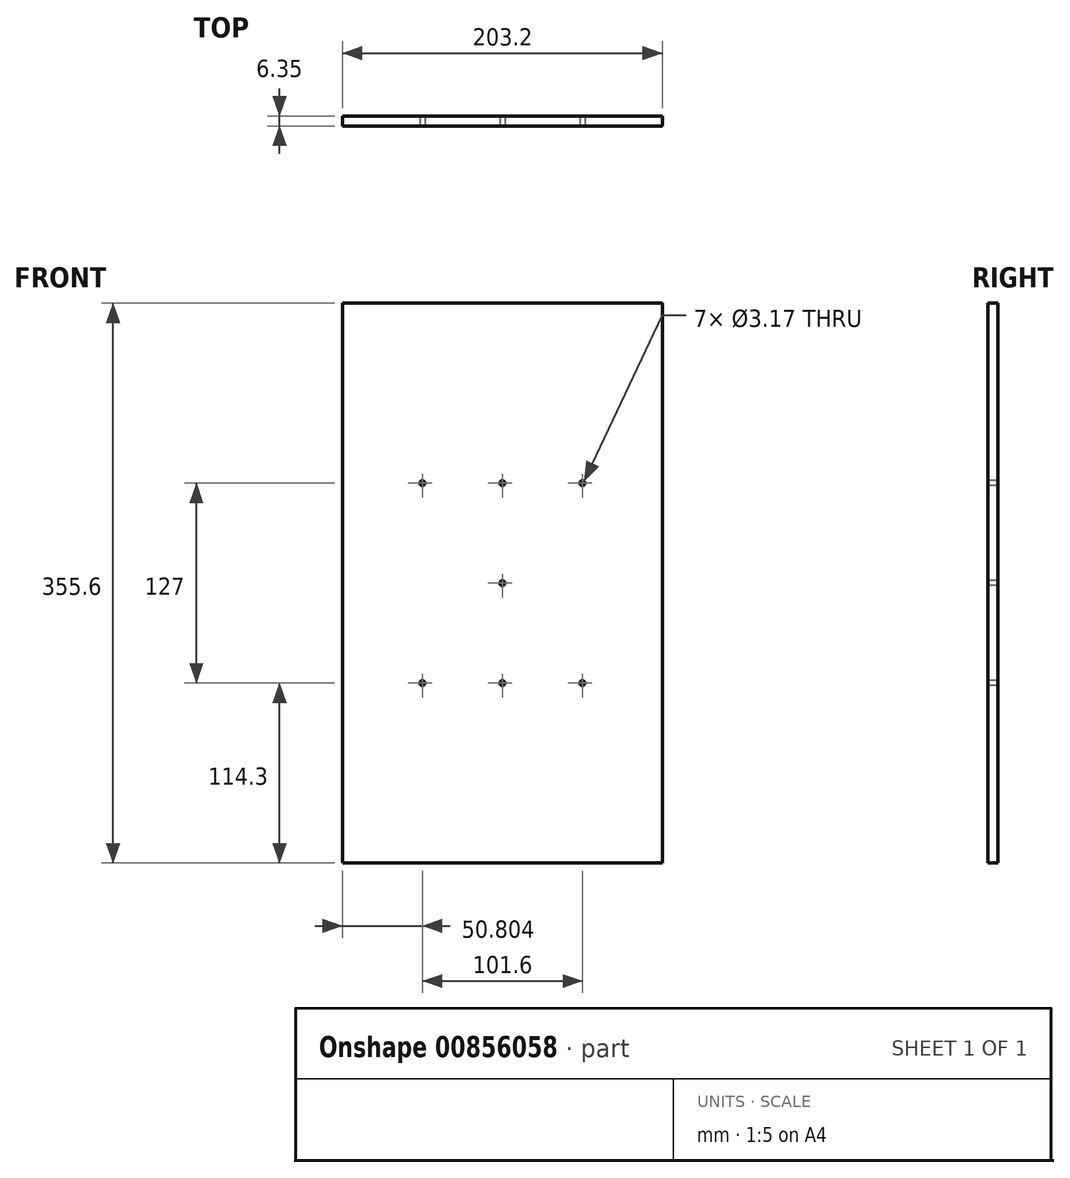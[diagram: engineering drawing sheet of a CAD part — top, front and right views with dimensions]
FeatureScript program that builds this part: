
annotation { "Feature Type Name" : "Feature", "Feature Type Description" : "" }
export const myFeature = defineFeature(function(context is Context, id is Id, definition is map)
    precondition{}
    {
        {
            var Q0;
            Q0=qCreatedBy(makeId("Front.planeOp"),FACE);
            var sketch = newSketch(context, id + "F0", { "sketchPlane" : qUnion([Q0])});
            skLineSegment(sketch, "E0.bottom", {"start": v(-103.34, 277.83) * mm, "end": v(99.86, 277.83) * mm});
            skLineSegment(sketch, "E0.top", {"start": v(-103.34, -77.77) * mm, "end": v(99.86, -77.77) * mm});
            skLineSegment(sketch, "E0.left", {"start": v(-103.34, 277.83) * mm, "end": v(-103.34, -77.77) * mm});
            skLineSegment(sketch, "E0.right", {"start": v(99.86, 277.83) * mm, "end": v(99.86, -77.77) * mm});
            skSolve(sketch);
        }
        {
            var Q0;
            Q0=makeQuery(id+"F0.imprint","IMPRINT",FACE,{"disambiguationData":[TD([[makeQuery(id+"F0.imprint","IMPRINT",EDGE,{"derivedFrom":sQuery(id+"F0.wireOp",EDGE,"E0.bottom")}),-1.0]])]});
            extrude(context, id + "F1", {"entities" : qUnion([Q0]), "depth" : 6.35 * mm, "offsetDistance" : 25.4 * mm});
        }
        {
            var Q0;
            Q0=makeQuery(id+"F1.opExtrude","CAP_FACE",FACE,{"disambiguationData":[OSD([sQuery(id+"F0.wireOp",EDGE,"E0.bottom"),sQuery(id+"F0.wireOp",EDGE,"E0.top"),sQuery(id+"F0.wireOp",EDGE,"E0.left"),sQuery(id+"F0.wireOp",EDGE,"E0.right")])],"isStart":false});
            var sketch = newSketch(context, id + "F2", { "sketchPlane" : qUnion([Q0])});
            skCircle(sketch, "E1", {"center": v(-1.74, 100.03) * mm, "radius": 1.59 * mm});
            skLineSegment(sketch, "E2", {"start": v(-1.74, 100.03) * mm, "end": v(-103.34, 100.03) * mm});
            skLineSegment(sketch, "E3", {"start": v(-1.74, 100.03) * mm, "end": v(99.86, 100.03) * mm});
            skCircle(sketch, "E4", {"center": v(-1.74, 163.53) * mm, "radius": 1.59 * mm});
            skCircle(sketch, "E5", {"center": v(-1.74, 36.53) * mm, "radius": 1.59 * mm});
            skLineSegment(sketch, "E6", {"start": v(-1.74, 163.53) * mm, "end": v(-1.74, 100.03) * mm});
            skLineSegment(sketch, "E7", {"start": v(-1.74, 100.03) * mm, "end": v(-1.74, 36.53) * mm});
            skCircle(sketch, "E8", {"center": v(-52.54, 163.53) * mm, "radius": 1.59 * mm});
            skCircle(sketch, "E9", {"center": v(49.06, 163.53) * mm, "radius": 1.59 * mm});
            skCircle(sketch, "E10", {"center": v(-52.54, 36.53) * mm, "radius": 1.59 * mm});
            skCircle(sketch, "E11", {"center": v(49.06, 36.53) * mm, "radius": 1.59 * mm});
            skLineSegment(sketch, "E12", {"start": v(-52.54, 163.53) * mm, "end": v(-103.34, 163.53) * mm});
            skLineSegment(sketch, "E13", {"start": v(-52.54, 163.53) * mm, "end": v(-1.74, 163.53) * mm});
            skLineSegment(sketch, "E14", {"start": v(-1.74, 163.53) * mm, "end": v(49.06, 163.53) * mm});
            skLineSegment(sketch, "E15", {"start": v(49.06, 163.53) * mm, "end": v(99.86, 163.53) * mm});
            skLineSegment(sketch, "E16", {"start": v(-52.54, 36.53) * mm, "end": v(-103.34, 36.53) * mm});
            skLineSegment(sketch, "E17", {"start": v(-52.54, 36.53) * mm, "end": v(-1.74, 36.53) * mm});
            skLineSegment(sketch, "E18", {"start": v(-1.74, 36.53) * mm, "end": v(49.06, 36.53) * mm});
            skLineSegment(sketch, "E19", {"start": v(49.06, 36.53) * mm, "end": v(99.86, 36.53) * mm});
            skLineSegment(sketch, "E20", {"start": v(-1.74, 163.53) * mm, "end": v(-1.74, 277.83) * mm});
            skLineSegment(sketch, "E21", {"start": v(-1.74, 36.53) * mm, "end": v(-1.74, -77.77) * mm});
            skSolve(sketch);
        }
        {
            var Q0;
            {var subQ0=sQuery(id+"F2.wireOp",EDGE,"E12");var subQ1=sQuery(id+"F2.wireOp",EDGE,"E8");var subQ2=makeQuery(id+"F2.imprint","INTERSECT",VERTEX,{"derivedFrom":[subQ1,subQ0]});Q0=makeQuery(id+"F2.imprint","IMPRINT",FACE,{"disambiguationData":[TD([[makeQuery(id+"F2.imprint","IMPRINT",EDGE,{"disambiguationData":[TD([[subQ2,1.0]])],"derivedFrom":subQ1}),1.0]])]});}
            var Q1;
            {var subQ0=sQuery(id+"F2.wireOp",EDGE,"E12");var subQ1=sQuery(id+"F2.wireOp",EDGE,"E8");var subQ2=makeQuery(id+"F2.imprint","INTERSECT",VERTEX,{"derivedFrom":[subQ1,subQ0]});Q1=makeQuery(id+"F2.imprint","IMPRINT",FACE,{"disambiguationData":[TD([[makeQuery(id+"F2.imprint","IMPRINT",EDGE,{"disambiguationData":[TD([[subQ2,-1.0]])],"derivedFrom":subQ1}),1.0]])]});}
            var Q2;
            {var subQ0=sQuery(id+"F2.wireOp",EDGE,"gXuljh3P-2iaE-ET4M-0B0z-znNCCFgcD3jr");var subQ1=sQuery(id+"F2.wireOp",EDGE,"E4");var subQ2=makeQuery(id+"F2.imprint","INTERSECT",VERTEX,{"derivedFrom":[subQ1,subQ0]});Q2=makeQuery(id+"F2.imprint","IMPRINT",FACE,{"disambiguationData":[TD([[makeQuery(id+"F2.imprint","IMPRINT",EDGE,{"disambiguationData":[TD([[subQ2,1.0]])],"derivedFrom":subQ1}),1.0]])]});}
            var Q3;
            {var subQ0=sQuery(id+"F2.wireOp",EDGE,"gXuljh3P-2iaE-ET4M-0B0z-znNCCFgcD3jr");var subQ1=sQuery(id+"F2.wireOp",EDGE,"E4");var subQ2=makeQuery(id+"F2.imprint","INTERSECT",VERTEX,{"derivedFrom":[subQ1,subQ0]});Q3=makeQuery(id+"F2.imprint","IMPRINT",FACE,{"disambiguationData":[TD([[makeQuery(id+"F2.imprint","IMPRINT",EDGE,{"disambiguationData":[TD([[subQ2,-1.0]])],"derivedFrom":subQ1}),1.0]])]});}
            var Q4;
            {var subQ0=sQuery(id+"F2.wireOp",EDGE,"E13");var subQ1=sQuery(id+"F2.wireOp",EDGE,"E4");var subQ2=makeQuery(id+"F2.imprint","INTERSECT",VERTEX,{"derivedFrom":[subQ1,subQ0]});Q4=makeQuery(id+"F2.imprint","IMPRINT",FACE,{"disambiguationData":[TD([[makeQuery(id+"F2.imprint","IMPRINT",EDGE,{"disambiguationData":[TD([[subQ2,-1.0]])],"derivedFrom":subQ1}),1.0]])]});}
            var Q5;
            {var subQ0=sQuery(id+"F2.wireOp",EDGE,"E14");var subQ1=sQuery(id+"F2.wireOp",EDGE,"E4");var subQ2=makeQuery(id+"F2.imprint","INTERSECT",VERTEX,{"derivedFrom":[subQ1,subQ0]});Q5=makeQuery(id+"F2.imprint","IMPRINT",FACE,{"disambiguationData":[TD([[makeQuery(id+"F2.imprint","IMPRINT",EDGE,{"disambiguationData":[TD([[subQ2,1.0]])],"derivedFrom":subQ1}),1.0]])]});}
            var Q6;
            {var subQ0=sQuery(id+"F2.wireOp",EDGE,"E14");var subQ1=sQuery(id+"F2.wireOp",EDGE,"E9");var subQ2=makeQuery(id+"F2.imprint","INTERSECT",VERTEX,{"derivedFrom":[subQ1,subQ0]});Q6=makeQuery(id+"F2.imprint","IMPRINT",FACE,{"disambiguationData":[TD([[makeQuery(id+"F2.imprint","IMPRINT",EDGE,{"disambiguationData":[TD([[subQ2,1.0]])],"derivedFrom":subQ1}),1.0]])]});}
            var Q7;
            {var subQ0=sQuery(id+"F2.wireOp",EDGE,"E14");var subQ1=sQuery(id+"F2.wireOp",EDGE,"E9");var subQ2=makeQuery(id+"F2.imprint","INTERSECT",VERTEX,{"derivedFrom":[subQ1,subQ0]});Q7=makeQuery(id+"F2.imprint","IMPRINT",FACE,{"disambiguationData":[TD([[makeQuery(id+"F2.imprint","IMPRINT",EDGE,{"disambiguationData":[TD([[subQ2,-1.0]])],"derivedFrom":subQ1}),1.0]])]});}
            var Q8;
            {var subQ0=sQuery(id+"F2.wireOp",EDGE,"E6");var subQ1=sQuery(id+"F2.wireOp",EDGE,"E1");var subQ2=makeQuery(id+"F2.imprint","INTERSECT",VERTEX,{"derivedFrom":[subQ1,subQ0]});Q8=makeQuery(id+"F2.imprint","IMPRINT",FACE,{"disambiguationData":[TD([[makeQuery(id+"F2.imprint","IMPRINT",EDGE,{"disambiguationData":[TD([[subQ2,-1.0]])],"derivedFrom":subQ1}),1.0]])]});}
            var Q9;
            {var subQ0=sQuery(id+"F2.wireOp",EDGE,"E6");var subQ1=sQuery(id+"F2.wireOp",EDGE,"E1");var subQ2=makeQuery(id+"F2.imprint","INTERSECT",VERTEX,{"derivedFrom":[subQ1,subQ0]});Q9=makeQuery(id+"F2.imprint","IMPRINT",FACE,{"disambiguationData":[TD([[makeQuery(id+"F2.imprint","IMPRINT",EDGE,{"disambiguationData":[TD([[subQ2,1.0]])],"derivedFrom":subQ1}),1.0]])]});}
            var Q10;
            {var subQ0=sQuery(id+"F2.wireOp",EDGE,"E3");var subQ1=sQuery(id+"F2.wireOp",EDGE,"E1");var subQ2=makeQuery(id+"F2.imprint","INTERSECT",VERTEX,{"derivedFrom":[subQ1,subQ0]});Q10=makeQuery(id+"F2.imprint","IMPRINT",FACE,{"disambiguationData":[TD([[makeQuery(id+"F2.imprint","IMPRINT",EDGE,{"disambiguationData":[TD([[subQ2,1.0]])],"derivedFrom":subQ1}),1.0]])]});}
            var Q11;
            {var subQ0=sQuery(id+"F2.wireOp",EDGE,"E2");var subQ1=sQuery(id+"F2.wireOp",EDGE,"E1");var subQ2=makeQuery(id+"F2.imprint","INTERSECT",VERTEX,{"derivedFrom":[subQ1,subQ0]});Q11=makeQuery(id+"F2.imprint","IMPRINT",FACE,{"disambiguationData":[TD([[makeQuery(id+"F2.imprint","IMPRINT",EDGE,{"disambiguationData":[TD([[subQ2,-1.0]])],"derivedFrom":subQ1}),1.0]])]});}
            var Q12;
            {var subQ0=sQuery(id+"F2.wireOp",EDGE,"E16");var subQ1=sQuery(id+"F2.wireOp",EDGE,"E10");var subQ2=makeQuery(id+"F2.imprint","INTERSECT",VERTEX,{"derivedFrom":[subQ1,subQ0]});Q12=makeQuery(id+"F2.imprint","IMPRINT",FACE,{"disambiguationData":[TD([[makeQuery(id+"F2.imprint","IMPRINT",EDGE,{"disambiguationData":[TD([[subQ2,1.0]])],"derivedFrom":subQ1}),1.0]])]});}
            var Q13;
            {var subQ0=sQuery(id+"F2.wireOp",EDGE,"E16");var subQ1=sQuery(id+"F2.wireOp",EDGE,"E10");var subQ2=makeQuery(id+"F2.imprint","INTERSECT",VERTEX,{"derivedFrom":[subQ1,subQ0]});Q13=makeQuery(id+"F2.imprint","IMPRINT",FACE,{"disambiguationData":[TD([[makeQuery(id+"F2.imprint","IMPRINT",EDGE,{"disambiguationData":[TD([[subQ2,-1.0]])],"derivedFrom":subQ1}),1.0]])]});}
            var Q14;
            {var subQ0=sQuery(id+"F2.wireOp",EDGE,"E7");var subQ1=sQuery(id+"F2.wireOp",EDGE,"E5");var subQ2=makeQuery(id+"F2.imprint","INTERSECT",VERTEX,{"derivedFrom":[subQ1,subQ0]});Q14=makeQuery(id+"F2.imprint","IMPRINT",FACE,{"disambiguationData":[TD([[makeQuery(id+"F2.imprint","IMPRINT",EDGE,{"disambiguationData":[TD([[subQ2,1.0]])],"derivedFrom":subQ1}),1.0]])]});}
            var Q15;
            {var subQ0=sQuery(id+"F2.wireOp",EDGE,"E7");var subQ1=sQuery(id+"F2.wireOp",EDGE,"E5");var subQ2=makeQuery(id+"F2.imprint","INTERSECT",VERTEX,{"derivedFrom":[subQ1,subQ0]});Q15=makeQuery(id+"F2.imprint","IMPRINT",FACE,{"disambiguationData":[TD([[makeQuery(id+"F2.imprint","IMPRINT",EDGE,{"disambiguationData":[TD([[subQ2,-1.0]])],"derivedFrom":subQ1}),1.0]])]});}
            var Q16;
            {var subQ0=sQuery(id+"F2.wireOp",EDGE,"E17");var subQ1=sQuery(id+"F2.wireOp",EDGE,"E5");var subQ2=makeQuery(id+"F2.imprint","INTERSECT",VERTEX,{"derivedFrom":[subQ1,subQ0]});Q16=makeQuery(id+"F2.imprint","IMPRINT",FACE,{"disambiguationData":[TD([[makeQuery(id+"F2.imprint","IMPRINT",EDGE,{"disambiguationData":[TD([[subQ2,-1.0]])],"derivedFrom":subQ1}),1.0]])]});}
            var Q17;
            {var subQ0=sQuery(id+"F2.wireOp",EDGE,"E18");var subQ1=sQuery(id+"F2.wireOp",EDGE,"E5");var subQ2=makeQuery(id+"F2.imprint","INTERSECT",VERTEX,{"derivedFrom":[subQ1,subQ0]});Q17=makeQuery(id+"F2.imprint","IMPRINT",FACE,{"disambiguationData":[TD([[makeQuery(id+"F2.imprint","IMPRINT",EDGE,{"disambiguationData":[TD([[subQ2,1.0]])],"derivedFrom":subQ1}),1.0]])]});}
            var Q18;
            {var subQ0=sQuery(id+"F2.wireOp",EDGE,"E18");var subQ1=sQuery(id+"F2.wireOp",EDGE,"E11");var subQ2=makeQuery(id+"F2.imprint","INTERSECT",VERTEX,{"derivedFrom":[subQ1,subQ0]});Q18=makeQuery(id+"F2.imprint","IMPRINT",FACE,{"disambiguationData":[TD([[makeQuery(id+"F2.imprint","IMPRINT",EDGE,{"disambiguationData":[TD([[subQ2,1.0]])],"derivedFrom":subQ1}),1.0]])]});}
            var Q19;
            {var subQ0=sQuery(id+"F2.wireOp",EDGE,"E18");var subQ1=sQuery(id+"F2.wireOp",EDGE,"E11");var subQ2=makeQuery(id+"F2.imprint","INTERSECT",VERTEX,{"derivedFrom":[subQ1,subQ0]});Q19=makeQuery(id+"F2.imprint","IMPRINT",FACE,{"disambiguationData":[TD([[makeQuery(id+"F2.imprint","IMPRINT",EDGE,{"disambiguationData":[TD([[subQ2,-1.0]])],"derivedFrom":subQ1}),1.0]])]});}
            extrude(context, id + "F3", {"entities" : qUnion([Q0, Q1, Q2, Q3, Q4, Q5, Q6, Q7, Q8, Q9, Q10, Q11, Q12, Q13, Q14, Q15, Q16, Q17, Q18, Q19]), "operationType" : NewBodyOperationType.REMOVE, "oppositeDirection" : true, "depth" : 25.4 * mm, "offsetDistance" : 25.4 * mm});
        }
    });
